# Revit family: Cordivari_LOLA
name_source: partatom
category: Mechanical Equipment
units: mm (PartAtom-declared; Revit-internal decimal feet)

## family parameters
Always vertical = Yes
Cut with Voids When Loaded = No
Host = Wall
OmniClass Number = 23.75.00.00
OmniClass Title = Climate Control (HVAC)
Part Type = Normal
Room Calculation Point = Yes
Round Connector Dimension = Use Diameter
Shared = No

## types (1)
- H_570 x L_1516 mm
    ACCESSORI ABBINATI = Kit valvola elegant lucida a squadra manuale - codice 5991990301084; Kit valvola elegant satinata interasse 50 mm a squadra dx con testa termostatica - codice 5991990320201; Kit 2 appendiabiti inox lucidi - codice 5991990010223; Kit 2 appendiabiti inox satinati - codice 5991990010224.
    ALTEZZA = 570 mm
    Assembly Code = D3040400
    CERTIFICATO BADGE = BIM.archiproducts.com_BADGE_.png
    COLORI DISPONIBILI = Radiatori e accessori: colore standard Bianco RAL 9010.
Per altri colori sovrapprezzo del 30%. Consultare tabella colori a pag. 208.
    CONTATTO AZIENDA = Tel. +39 085.80.40.1 Fax +39 085.80.41.418
    CONTENUTO D'ACQUA RADIATORE lt = 5.1 $
    DISTANZA DAL MURO = 80 mm
    Default Elevation = 0 mm  [stored 0 ft]
    Description = Benessere e relax prendono forma nelle linee sinuose ed avvolgenti del radiatore Lola. Impossibile non restare incantati dai giochi di luce che scivolano dai radianti inox. La particolare finitura a specchio aggiunge valore estetico in tutti gli ambienti, classici e moderni.
    Distanza = 80 mm
    Distanza dal muro consentita = 81 <d> 68
    INTERASSE = 1450 mm
    LARGHEZZA = 1516 mm
    Manufacturer = CORDIVARI
    Materiale = Acciaio inox, Satinato
    Model = LOLA ORIZZONTALE
    N° ELEMENTI = 14
    PESO RADIATORE A VUOTO kg = 19
    PRESSIONE MAX bar = 8
    RESA RADIATORE Δt 50° w = 698 $
    URL = http://www.archiproducts.com
    URL SCHEDA TECNICA = http://www.cordivari.it

note: [stored X ft] marks values corroborated as IEEE doubles in the binary element streams (Revit-internal decimal feet)
